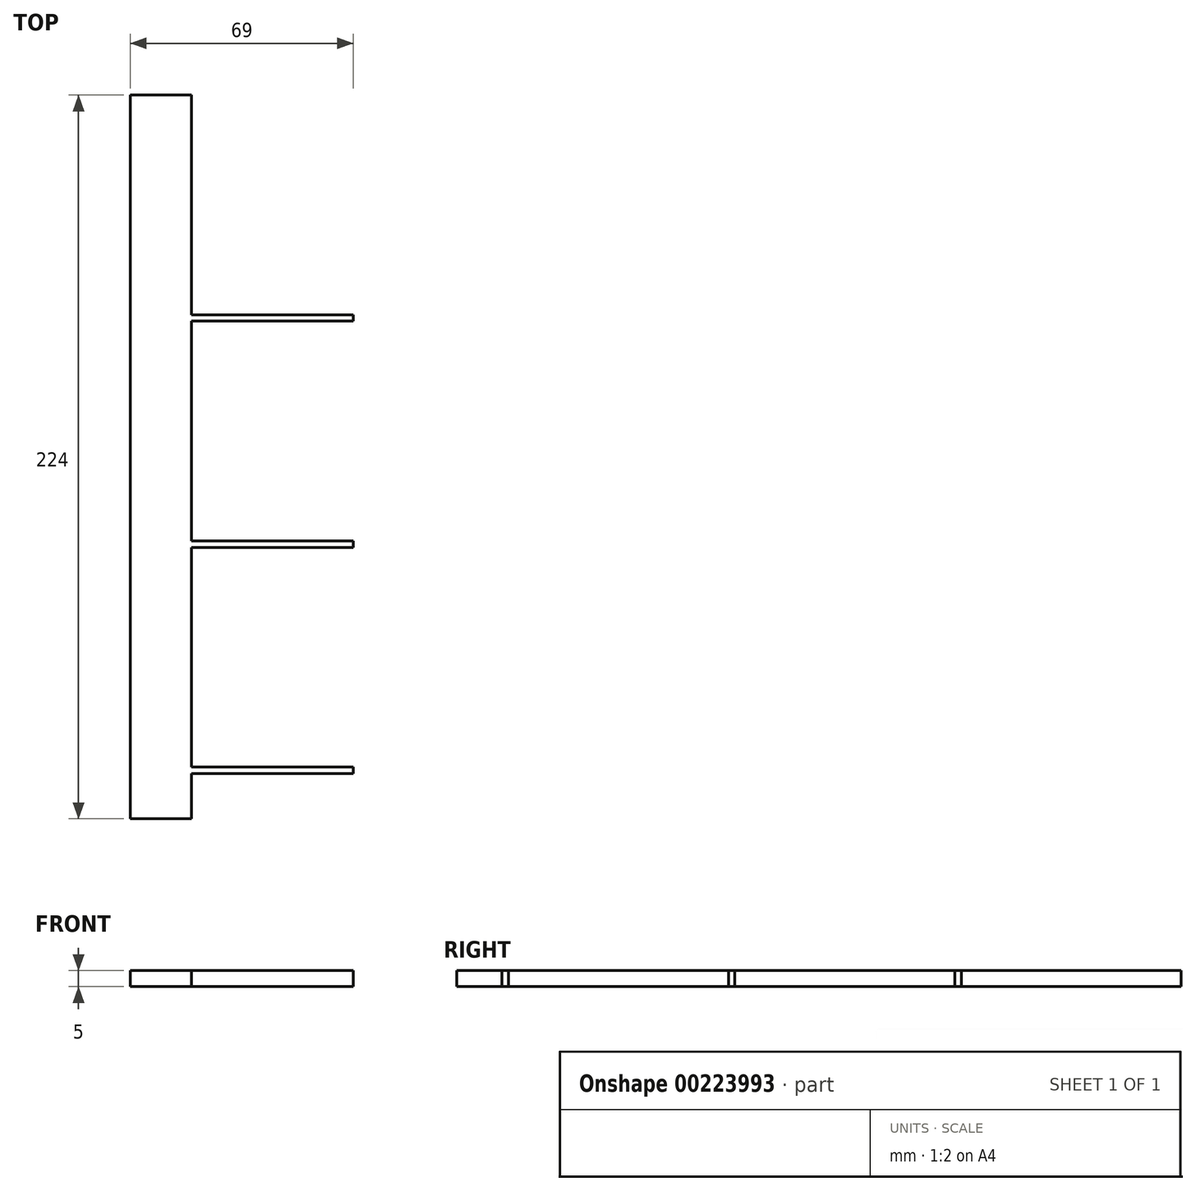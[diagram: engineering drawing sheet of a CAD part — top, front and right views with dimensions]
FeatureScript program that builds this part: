
annotation { "Feature Type Name" : "Feature", "Feature Type Description" : "" }
export const myFeature = defineFeature(function(context is Context, id is Id, definition is map)
    precondition{}
    {
        {
            var Q0;
            Q0=qCreatedBy(makeId("Top.planeOp"),FACE);
            var sketch = newSketch(context, id + "F0", { "sketchPlane" : qUnion([Q0])});
            skLineSegment(sketch, "E0.bottom", {"start": v(9.5, -112) * mm, "end": v(-9.5, -112) * mm});
            skLineSegment(sketch, "E0.top", {"start": v(9.5, 112) * mm, "end": v(-9.5, 112) * mm});
            skLineSegment(sketch, "E0.left", {"start": v(9.5, -112) * mm, "end": v(9.5, -98) * mm});
            skLineSegment(sketch, "E0.right", {"start": v(-9.5, -112) * mm, "end": v(-9.5, 112) * mm});
            skPoint(sketch, "E0.middle", {"position": v(0, 0) * mm});
            skLineSegment(sketch, "E1.bottom", {"start": v(9.5, -96) * mm, "end": v(59.5, -96) * mm});
            skLineSegment(sketch, "E1.top", {"start": v(9.5, -98) * mm, "end": v(59.5, -98) * mm});
            skLineSegment(sketch, "E1.right", {"start": v(59.5, -96) * mm, "end": v(59.5, -98) * mm});
            skLineSegment(sketch, "E2.bottom", {"start": v(9.5, -28) * mm, "end": v(59.5, -28) * mm});
            skLineSegment(sketch, "E2.top", {"start": v(9.5, -26) * mm, "end": v(59.5, -26) * mm});
            skLineSegment(sketch, "E2.right", {"start": v(59.5, -28) * mm, "end": v(59.5, -26) * mm});
            skLineSegment(sketch, "E3.bottom", {"start": v(9.5, 44) * mm, "end": v(59.5, 44) * mm});
            skLineSegment(sketch, "E3.top", {"start": v(9.5, 42) * mm, "end": v(59.5, 42) * mm});
            skLineSegment(sketch, "E3.right", {"start": v(59.5, 44) * mm, "end": v(59.5, 42) * mm});
            skLineSegment(sketch, "E4", {"start": v(9.5, -112) * mm, "end": v(59.5, -112) * mm, "construction": true});
            skLineSegment(sketch, "E5", {"start": v(9.5, 112) * mm, "end": v(59.5, 112) * mm, "construction": true});
            skLineSegment(sketch, "E6", {"start": v(34.5, 112) * mm, "end": v(34.5, 44) * mm, "construction": true});
            skLineSegment(sketch, "E7.trimOffspring", {"start": v(9.5, 44) * mm, "end": v(9.5, 112) * mm});
            skLineSegment(sketch, "E8.trimOffspring", {"start": v(9.5, -26) * mm, "end": v(9.5, 42) * mm});
            skLineSegment(sketch, "E9.trimOffspring", {"start": v(9.5, -96) * mm, "end": v(9.5, -28) * mm});
            skLineSegment(sketch, "E10", {"start": v(34.5, -96) * mm, "end": v(34.5, -28) * mm, "construction": true});
            skLineSegment(sketch, "E11", {"start": v(34.5, -26) * mm, "end": v(34.5, 42) * mm, "construction": true});
            skSolve(sketch);
        }
        {
            var Q0;
            Q0 = qSketchRegion(id + "F0", true);
            extrude(context, id + "F1", {"entities" : qUnion([Q0]), "depth" : 5 * mm});
        }
    });
